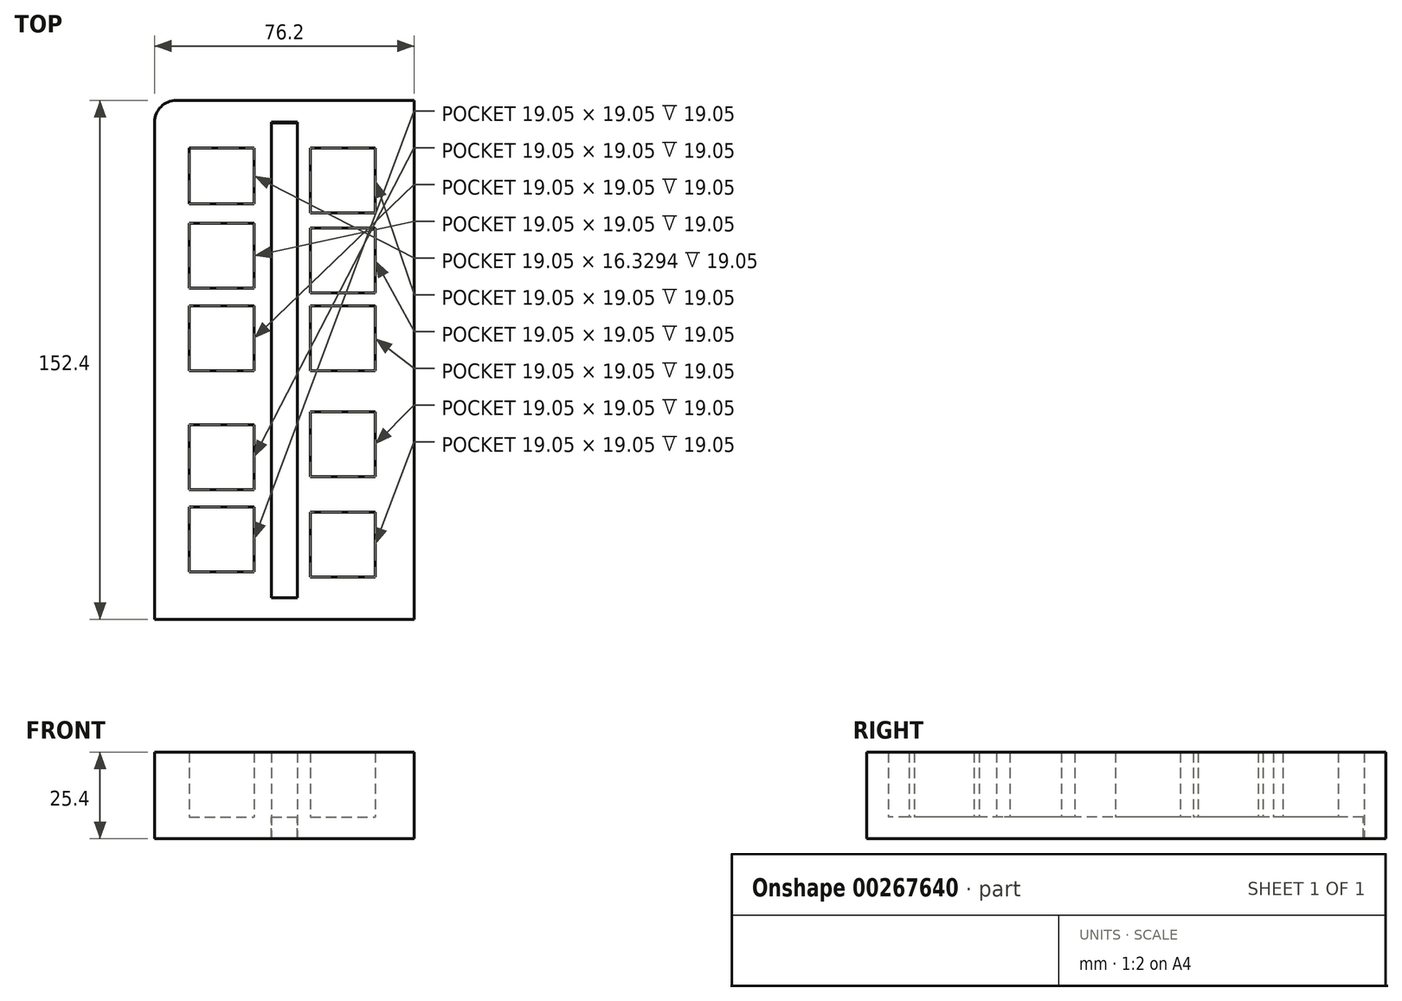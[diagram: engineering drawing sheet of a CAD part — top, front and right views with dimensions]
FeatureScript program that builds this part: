
annotation { "Feature Type Name" : "Feature", "Feature Type Description" : "" }
export const myFeature = defineFeature(function(context is Context, id is Id, definition is map)
    precondition{}
    {
        {
            var Q0;
            Q0=qCreatedBy(makeId("Top.planeOp"),FACE);
            var sketch = newSketch(context, id + "F0", { "sketchPlane" : qUnion([Q0])});
            skLineSegment(sketch, "E0.bottom", {"start": v(-31.75, 76.2) * mm, "end": v(38.1, 76.2) * mm});
            skLineSegment(sketch, "E0.top", {"start": v(-38.1, -76.2) * mm, "end": v(38.1, -76.2) * mm});
            skLineSegment(sketch, "E0.left", {"start": v(-38.1, 69.85) * mm, "end": v(-38.1, -76.2) * mm});
            skLineSegment(sketch, "E0.right", {"start": v(38.1, 76.2) * mm, "end": v(38.1, -76.2) * mm});
            skPoint(sketch, "E0.middle", {"position": v(0, 0) * mm});
            skLineSegment(sketch, "E1.bottom", {"start": v(-31.75, 69.85) * mm, "end": v(31.75, 69.85) * mm});
            skLineSegment(sketch, "E1.top", {"start": v(-31.75, -69.85) * mm, "end": v(31.75, -69.85) * mm});
            skLineSegment(sketch, "E1.left", {"start": v(-31.75, 69.85) * mm, "end": v(-31.75, -69.85) * mm});
            skLineSegment(sketch, "E1.right", {"start": v(31.75, 69.85) * mm, "end": v(31.75, -69.85) * mm});
            skPoint(sketch, "E2.visualSharp", {"position": v(-31.75, 69.85) * mm});
            skLineSegment(sketch, "E2.filletArc", {"start": v(-31.75, 69.85) * mm, "end": v(-31.75, 69.85) * mm});
            skPoint(sketch, "E3.visualSharp", {"position": v(-38.1, 76.2) * mm});
            skArc(sketch, "E3.filletArc", {"start": v(-31.75, 76.2) * mm, "mid": v(-36.24, 74.34) * mm, "end": v(-38.1, 69.85) * mm});
            skPoint(sketch, "E4.visualSharp", {"position": v(31.75, 69.85) * mm});
            skLineSegment(sketch, "E4.filletArc", {"start": v(31.75, 69.85) * mm, "end": v(31.75, 69.85) * mm});
            skPoint(sketch, "E5.visualSharp", {"position": v(38.1, 76.2) * mm});
            skLineSegment(sketch, "E5.filletArc", {"start": v(38.1, 76.2) * mm, "end": v(38.1, 76.2) * mm});
            skPoint(sketch, "E6.visualSharp", {"position": v(31.75, -69.85) * mm});
            skLineSegment(sketch, "E6.filletArc", {"start": v(31.75, -69.85) * mm, "end": v(31.75, -69.85) * mm});
            skPoint(sketch, "E7.visualSharp", {"position": v(38.1, -76.2) * mm});
            skLineSegment(sketch, "E7.filletArc", {"start": v(38.1, -76.2) * mm, "end": v(38.1, -76.2) * mm});
            skPoint(sketch, "E8.visualSharp", {"position": v(-38.1, -76.2) * mm});
            skLineSegment(sketch, "E8.filletArc", {"start": v(-38.1, -76.2) * mm, "end": v(-38.1, -76.2) * mm});
            skPoint(sketch, "E9.visualSharp", {"position": v(-31.75, -69.85) * mm});
            skLineSegment(sketch, "E9.filletArc", {"start": v(-31.75, -69.85) * mm, "end": v(-31.75, -69.85) * mm});
            skLineSegment(sketch, "E10.bottom", {"start": v(-3.81, 69.85) * mm, "end": v(3.81, 69.85) * mm});
            skLineSegment(sketch, "E10.top", {"start": v(-3.81, -69.85) * mm, "end": v(3.81, -69.85) * mm});
            skLineSegment(sketch, "E10.left", {"start": v(-3.81, 69.85) * mm, "end": v(-3.81, -69.85) * mm});
            skLineSegment(sketch, "E10.right", {"start": v(3.81, 69.85) * mm, "end": v(3.81, -69.85) * mm});
            skLineSegment(sketch, "E11.bottom", {"start": v(-27.94, 62.23) * mm, "end": v(-8.9, 62.23) * mm});
            skLineSegment(sketch, "E11.top", {"start": v(-27.94, 45.9) * mm, "end": v(-8.89, 45.9) * mm});
            skLineSegment(sketch, "E11.left", {"start": v(-27.94, 62.23) * mm, "end": v(-27.94, 45.9) * mm});
            skLineSegment(sketch, "E11.right", {"start": v(-8.9, 62.23) * mm, "end": v(-8.9, 45.9) * mm});
            skLineSegment(sketch, "E12.bottom", {"start": v(-27.94, 40.07) * mm, "end": v(-8.89, 40.07) * mm});
            skLineSegment(sketch, "E12.top", {"start": v(-27.94, 21.02) * mm, "end": v(-8.89, 21.02) * mm});
            skLineSegment(sketch, "E12.left", {"start": v(-27.94, 40.07) * mm, "end": v(-27.94, 21.02) * mm});
            skLineSegment(sketch, "E12.right", {"start": v(-8.89, 40.07) * mm, "end": v(-8.89, 21.02) * mm});
            skLineSegment(sketch, "E13.bottom", {"start": v(-27.94, 15.88) * mm, "end": v(-8.89, 15.88) * mm});
            skLineSegment(sketch, "E13.top", {"start": v(-27.94, -3.17) * mm, "end": v(-8.89, -3.17) * mm});
            skLineSegment(sketch, "E13.left", {"start": v(-27.94, 15.88) * mm, "end": v(-27.94, -3.17) * mm});
            skLineSegment(sketch, "E13.right", {"start": v(-8.89, 15.88) * mm, "end": v(-8.89, -3.17) * mm});
            skLineSegment(sketch, "E14.bottom", {"start": v(-27.94, -19.05) * mm, "end": v(-8.89, -19.05) * mm});
            skLineSegment(sketch, "E14.top", {"start": v(-27.94, -38.1) * mm, "end": v(-8.89, -38.1) * mm});
            skLineSegment(sketch, "E14.left", {"start": v(-27.94, -19.05) * mm, "end": v(-27.94, -38.1) * mm});
            skLineSegment(sketch, "E14.right", {"start": v(-8.89, -19.05) * mm, "end": v(-8.89, -38.1) * mm});
            skLineSegment(sketch, "E15.bottom", {"start": v(-27.94, -43.18) * mm, "end": v(-8.89, -43.18) * mm});
            skLineSegment(sketch, "E15.top", {"start": v(-27.94, -62.23) * mm, "end": v(-8.89, -62.23) * mm});
            skLineSegment(sketch, "E15.left", {"start": v(-27.94, -43.18) * mm, "end": v(-27.94, -62.23) * mm});
            skLineSegment(sketch, "E15.right", {"start": v(-8.89, -43.18) * mm, "end": v(-8.89, -62.23) * mm});
            skLineSegment(sketch, "E16.bottom", {"start": v(7.62, 62.23) * mm, "end": v(26.67, 62.23) * mm});
            skLineSegment(sketch, "E16.top", {"start": v(7.62, 43.18) * mm, "end": v(26.67, 43.18) * mm});
            skLineSegment(sketch, "E16.left", {"start": v(7.62, 62.23) * mm, "end": v(7.62, 43.18) * mm});
            skLineSegment(sketch, "E16.right", {"start": v(26.67, 62.23) * mm, "end": v(26.67, 43.18) * mm});
            skLineSegment(sketch, "E17.bottom", {"start": v(7.62, 38.72) * mm, "end": v(26.67, 38.72) * mm});
            skLineSegment(sketch, "E17.top", {"start": v(7.62, 19.67) * mm, "end": v(26.67, 19.67) * mm});
            skLineSegment(sketch, "E17.left", {"start": v(7.62, 38.72) * mm, "end": v(7.62, 19.67) * mm});
            skLineSegment(sketch, "E17.right", {"start": v(26.67, 38.72) * mm, "end": v(26.67, 19.67) * mm});
            skLineSegment(sketch, "E18.bottom", {"start": v(7.62, 15.87) * mm, "end": v(26.67, 15.88) * mm});
            skLineSegment(sketch, "E18.top", {"start": v(7.62, -3.18) * mm, "end": v(26.67, -3.17) * mm});
            skLineSegment(sketch, "E18.left", {"start": v(7.62, 15.88) * mm, "end": v(7.62, -3.18) * mm});
            skLineSegment(sketch, "E18.right", {"start": v(26.67, 15.88) * mm, "end": v(26.67, -3.17) * mm});
            skLineSegment(sketch, "E19.bottom", {"start": v(7.62, -15.23) * mm, "end": v(26.67, -15.23) * mm});
            skLineSegment(sketch, "E19.top", {"start": v(7.62, -34.28) * mm, "end": v(26.67, -34.28) * mm});
            skLineSegment(sketch, "E19.left", {"start": v(7.62, -15.23) * mm, "end": v(7.62, -34.28) * mm});
            skLineSegment(sketch, "E19.right", {"start": v(26.67, -15.23) * mm, "end": v(26.67, -34.28) * mm});
            skLineSegment(sketch, "E20.bottom", {"start": v(7.62, -44.75) * mm, "end": v(26.67, -44.75) * mm});
            skLineSegment(sketch, "E20.top", {"start": v(7.62, -63.8) * mm, "end": v(26.67, -63.8) * mm});
            skLineSegment(sketch, "E20.left", {"start": v(7.62, -44.75) * mm, "end": v(7.62, -63.8) * mm});
            skLineSegment(sketch, "E20.right", {"start": v(26.67, -44.75) * mm, "end": v(26.67, -63.8) * mm});
            skLineSegment(sketch, "E21.bottom", {"start": v(38.1, 76.2) * mm, "end": v(-38.1, 76.2) * mm});
            skLineSegment(sketch, "E21.top", {"start": v(38.1, -76.2) * mm, "end": v(-38.1, -76.2) * mm});
            skLineSegment(sketch, "E21.right", {"start": v(-38.1, 76.2) * mm, "end": v(-38.1, -76.2) * mm});
            skLineSegment(sketch, "E22.top", {"start": v(-38.1, 76.2) * mm, "end": v(38.1, 76.2) * mm});
            skLineSegment(sketch, "E22.left", {"start": v(-38.1, -76.2) * mm, "end": v(-38.1, 76.2) * mm});
            skLineSegment(sketch, "E22.right", {"start": v(38.1, -76.2) * mm, "end": v(38.1, 76.2) * mm});
            skSolve(sketch);
        }
        {
            var Q0;
            Q0=makeQuery(id+"F0.imprint","IMPRINT",FACE,{"disambiguationData":[TD([[makeQuery(id+"F0.imprint","IMPRINT",EDGE,{"derivedFrom":sQuery(id+"F0.wireOp",EDGE,"E10.bottom")}),-1.0]])]});
            var Q1;
            {var subQ1=sQuery(id+"F0.wireOp",EDGE,"E1.left");Q1=makeQuery(id+"F0.imprint","IMPRINT",FACE,{"disambiguationData":[TD([[makeQuery(id+"F0.imprint","IMPRINT",EDGE,{"derivedFrom":subQ1}),1.0]])]});}
            var Q2;
            {var subQ1=sQuery(id+"F0.wireOp",EDGE,"E1.right");Q2=makeQuery(id+"F0.imprint","IMPRINT",FACE,{"disambiguationData":[TD([[makeQuery(id+"F0.imprint","IMPRINT",EDGE,{"derivedFrom":subQ1}),-1.0]])]});}
            var Q3;
            Q3=makeQuery(id+"F0.imprint","IMPRINT",FACE,{"disambiguationData":[TD([[makeQuery(id+"F0.imprint","IMPRINT",EDGE,{"derivedFrom":sQuery(id+"F0.wireOp",EDGE,"E0.bottom")}),-1.0]])]});
            extrude(context, id + "F1", {"entities" : qUnion([Q0, Q1, Q2, Q3]), "depth" : 25.4 * mm});
        }
        {
            var Q0;
            Q0=qCreatedBy(makeId("Top.planeOp"),FACE);
            var sketch = newSketch(context, id + "F2", { "sketchPlane" : qUnion([Q0])});
            skLineSegment(sketch, "E23.bottom", {"start": v(-32.12, -69.96) * mm, "end": v(32.32, -69.96) * mm});
            skLineSegment(sketch, "E23.top", {"start": v(-32.12, 69.57) * mm, "end": v(32.32, 69.57) * mm});
            skLineSegment(sketch, "E23.left", {"start": v(-32.12, -69.96) * mm, "end": v(-32.12, 69.57) * mm});
            skLineSegment(sketch, "E23.right", {"start": v(32.32, -69.96) * mm, "end": v(32.32, 69.57) * mm});
            skSolve(sketch);
        }
        {
            var Q0;
            Q0 = qSketchRegion(id + "F2", true);
            extrude(context, id + "F3", {"entities" : qUnion([Q0]), "operationType" : NewBodyOperationType.ADD, "depth" : 6.35 * mm});
        }
    });
